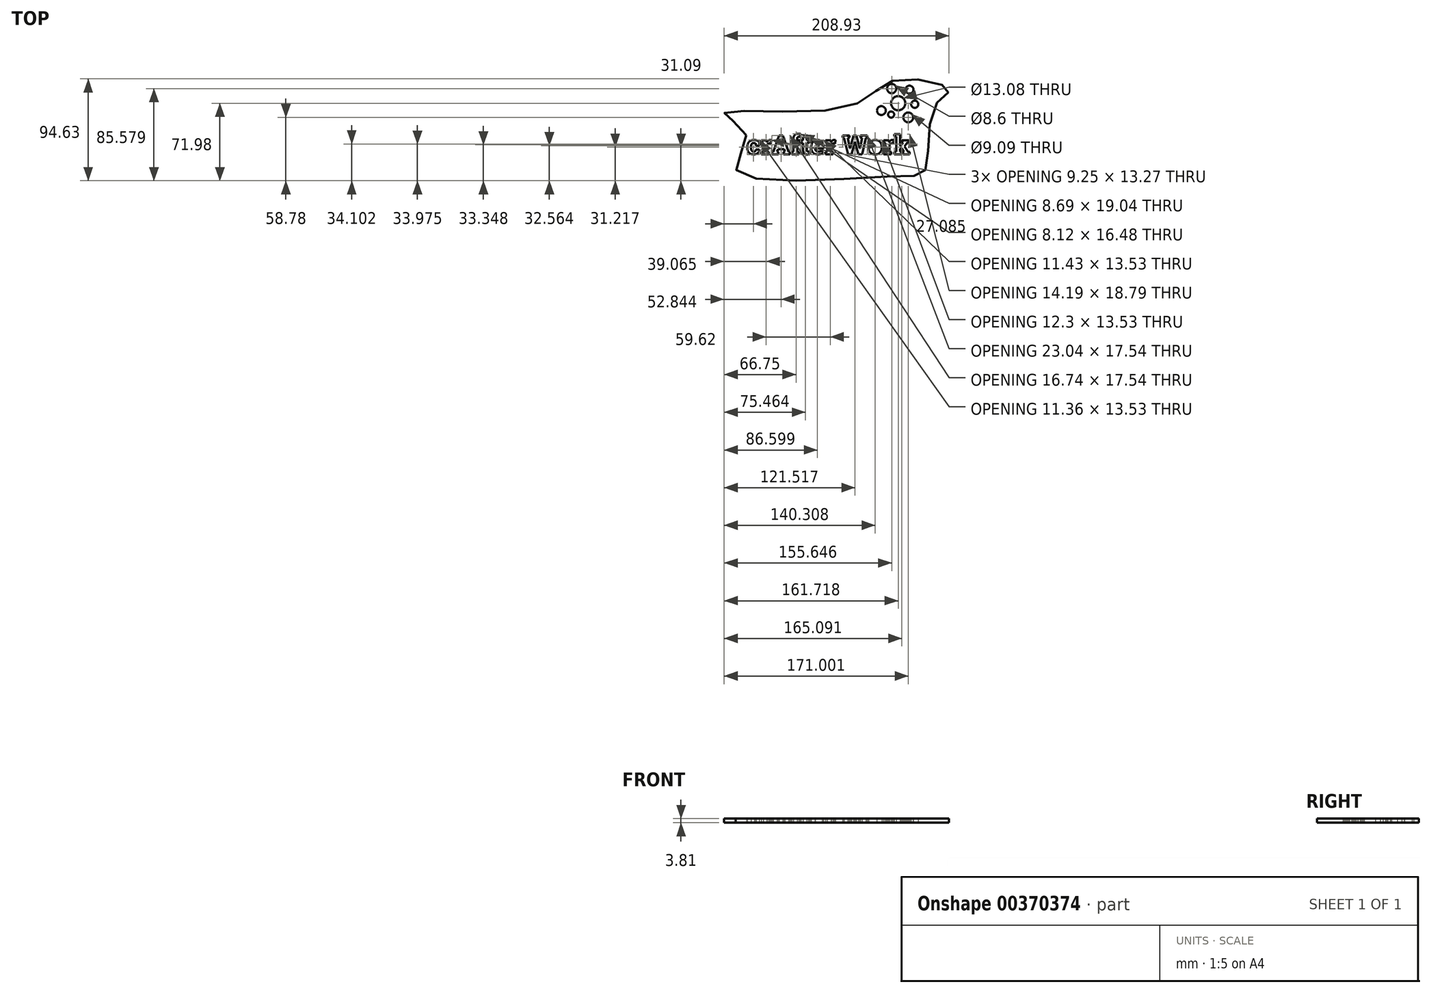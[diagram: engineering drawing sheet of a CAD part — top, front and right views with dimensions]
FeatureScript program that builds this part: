
annotation { "Feature Type Name" : "Feature", "Feature Type Description" : "" }
export const myFeature = defineFeature(function(context is Context, id is Id, definition is map)
    precondition{}
    {
        {
            var Q0;
            Q0=qCreatedBy(makeId("Top.planeOp"),FACE);
            var sketch = newSketch(context, id + "F0", { "sketchPlane" : qUnion([Q0])});
            skText(sketch, "E0", { "text": "crAfter Work", "fontName": "RobotoSlab-Bold.ttf"});
            skFitSpline(sketch, "E1", {"points": [v(-46.64, 0) * mm, v(-67.23, 20.13) * mm, v(47.47, 26.2) * mm, v(91.94, 51.26) * mm, v(141.53, 42.21) * mm, v(128.74, 27.53) * mm, v(120.22, -30.86) * mm, v(94.95, -38.16) * mm, v(-55.8, -32.82) * mm, v(-46.64, 0) * mm]});
            skCircle(sketch, "E2", {"center": v(94.48, 29.64) * mm, "radius": 6.54 * mm});
            skCircle(sketch, "E3", {"center": v(78.82, 22.81) * mm, "radius": 4.09 * mm});
            skCircle(sketch, "E4", {"center": v(88.4, 43.24) * mm, "radius": 4.3 * mm});
            skCircle(sketch, "E5", {"center": v(104.99, 42.26) * mm, "radius": 3.66 * mm});
            skCircle(sketch, "E6", {"center": v(109.82, 28.68) * mm, "radius": 3.34 * mm});
            skCircle(sketch, "E7", {"center": v(103.76, 16.44) * mm, "radius": 4.55 * mm});
            skCircle(sketch, "E8", {"center": v(87.9, 19.12) * mm, "radius": 2.85 * mm});
            const initialGuessF0  = {"E0": [-0.04664, -0.01776, 1, 0, 0.01776]};
            skSetInitialGuess(sketch, initialGuessF0);
            skSolve(sketch);
        }
        {
            var Q0;
            Q0=makeQuery(id+"F0.imprint","IMPRINT",FACE,{"disambiguationData":[TD([[makeQuery(id+"F0.imprint","IMPRINT",EDGE,{"derivedFrom":sQuery(id+"F0.wireOp",EDGE,"E0.sketch_text.stroke-0")}),1.0]])]});
            extrude(context, id + "F1", {"entities" : qUnion([Q0]), "depth" : 3.8 * mm});
        }
    });
